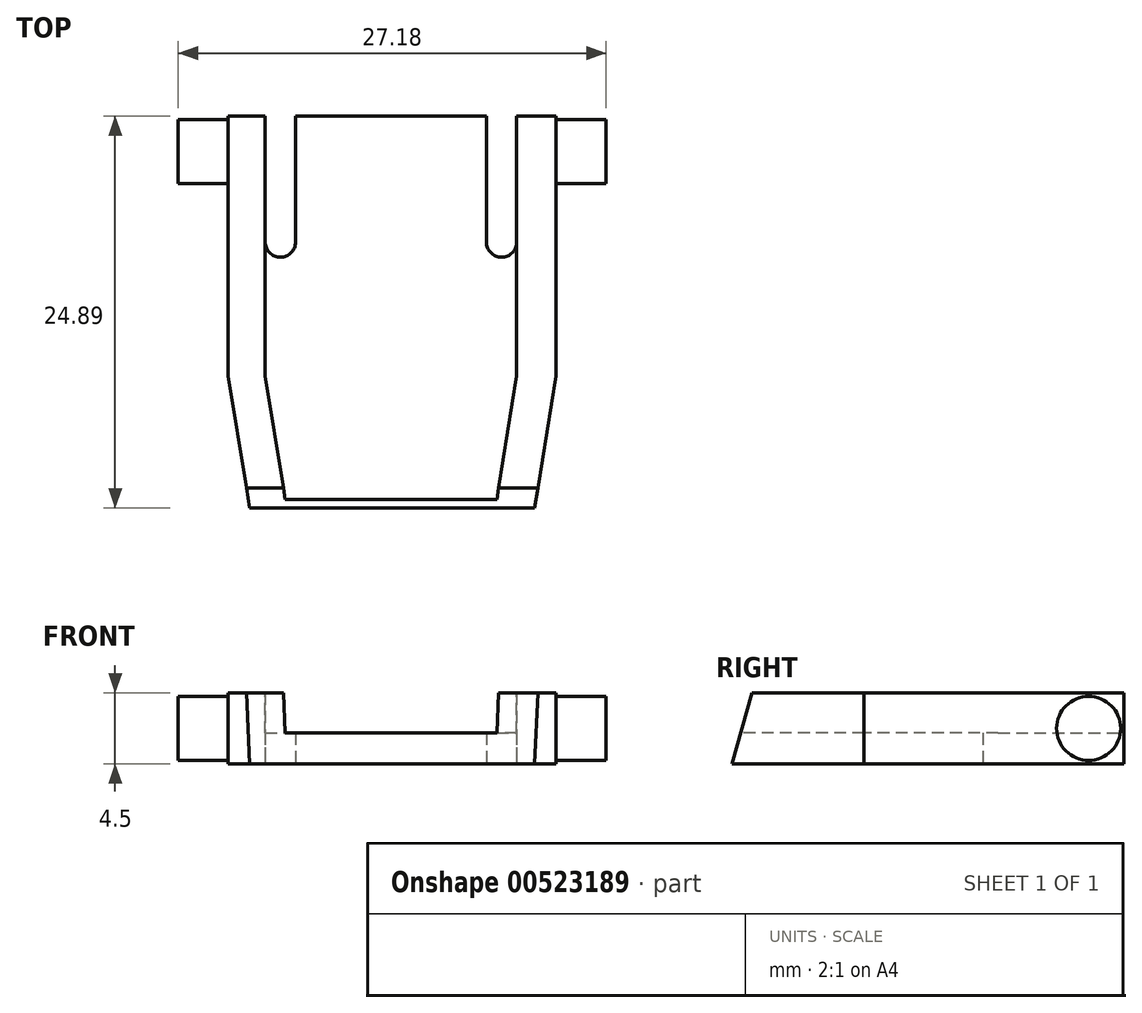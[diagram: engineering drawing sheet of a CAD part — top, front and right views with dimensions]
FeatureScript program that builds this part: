
annotation { "Feature Type Name" : "Feature", "Feature Type Description" : "" }
export const myFeature = defineFeature(function(context is Context, id is Id, definition is map)
    precondition{}
    {
        {
            var Q0;
            Q0=qCreatedBy(makeId("Top.planeOp"),FACE);
            var sketch = newSketch(context, id + "F0", { "sketchPlane" : qUnion([Q0])});
            skLineSegment(sketch, "E0.bottom", {"start": v(-13.75, -0.3) * mm, "end": v(-10.25, -0.3) * mm});
            skLineSegment(sketch, "E0.right", {"start": v(-10.25, -0.3) * mm, "end": v(-10.25, -18.09) * mm});
            skLineSegment(sketch, "E1.bottom", {"start": v(14.07, -0.3) * mm, "end": v(10.57, -0.3) * mm});
            skLineSegment(sketch, "E1.right", {"start": v(10.57, -0.3) * mm, "end": v(10.57, -18.09) * mm});
            skLineSegment(sketch, "E2.top", {"start": v(-6.94, -2.16) * mm, "end": v(-6.94, -2.16) * mm});
            skLineSegment(sketch, "E2.left", {"start": v(-7.9, 6.8) * mm, "end": v(-7.9, -1.2) * mm});
            skLineSegment(sketch, "E2.right", {"start": v(-5.97, 6.8) * mm, "end": v(-5.97, -1.2) * mm});
            skLineSegment(sketch, "E3.bottom", {"start": v(7.1, -2.16) * mm, "end": v(7.1, -2.16) * mm});
            skLineSegment(sketch, "E3.left", {"start": v(6.14, -1.2) * mm, "end": v(6.14, 6.8) * mm});
            skLineSegment(sketch, "E3.right", {"start": v(8.07, -1.2) * mm, "end": v(8.07, 6.8) * mm});
            skLineSegment(sketch, "E4", {"start": v(-13.75, 6.8) * mm, "end": v(-7.9, 6.8) * mm});
            skLineSegment(sketch, "E5", {"start": v(8.07, 6.8) * mm, "end": v(14.07, 6.8) * mm});
            skLineSegment(sketch, "E6", {"start": v(-5.97, 6.8) * mm, "end": v(6.14, 6.8) * mm});
            skLineSegment(sketch, "E7", {"start": v(14.07, 6.8) * mm, "end": v(14.07, -0.3) * mm});
            skLineSegment(sketch, "E8", {"start": v(-13.75, -0.3) * mm, "end": v(-13.75, 6.8) * mm});
            skLineSegment(sketch, "E9", {"start": v(-10.25, -9.7) * mm, "end": v(-8.9, -18.09) * mm});
            skLineSegment(sketch, "E10", {"start": v(-8.9, -18.09) * mm, "end": v(9.21, -18.09) * mm});
            skLineSegment(sketch, "E11", {"start": v(9.21, -18.09) * mm, "end": v(10.57, -9.7) * mm});
            skLineSegment(sketch, "E12", {"start": v(9.21, -18.09) * mm, "end": v(10.57, -18.09) * mm});
            skLineSegment(sketch, "E13", {"start": v(-8.9, -18.09) * mm, "end": v(-10.25, -18.09) * mm});
            skLineSegment(sketch, "E14.bottom", {"start": v(10.57, 6.8) * mm, "end": v(14.07, 6.8) * mm});
            skLineSegment(sketch, "E14.top", {"start": v(10.57, 5.97) * mm, "end": v(14.07, 5.97) * mm});
            skLineSegment(sketch, "E14.left", {"start": v(10.57, 6.8) * mm, "end": v(10.57, 5.97) * mm});
            skLineSegment(sketch, "E14.right", {"start": v(14.07, 6.8) * mm, "end": v(14.07, 5.97) * mm});
            skLineSegment(sketch, "E15.bottom", {"start": v(-13.75, 5.97) * mm, "end": v(-10.25, 5.97) * mm});
            skLineSegment(sketch, "E15.top", {"start": v(-13.75, 6.8) * mm, "end": v(-10.25, 6.8) * mm});
            skLineSegment(sketch, "E15.left", {"start": v(-13.75, 5.97) * mm, "end": v(-13.75, 6.8) * mm});
            skLineSegment(sketch, "E15.right", {"start": v(-10.25, 5.97) * mm, "end": v(-10.25, 6.8) * mm});
            skPoint(sketch, "E16.visualSharp", {"position": v(-7.9, -2.16) * mm});
            skArc(sketch, "E16.filletArc", {"start": v(-7.9, -1.2) * mm, "mid": v(-7.62, -1.88) * mm, "end": v(-6.94, -2.16) * mm});
            skPoint(sketch, "E17.visualSharp", {"position": v(-5.97, -2.16) * mm});
            skArc(sketch, "E17.filletArc", {"start": v(-6.94, -2.16) * mm, "mid": v(-6.26, -1.88) * mm, "end": v(-5.97, -1.2) * mm});
            skPoint(sketch, "E18.visualSharp", {"position": v(6.14, -2.16) * mm});
            skArc(sketch, "E18.filletArc", {"start": v(6.14, -1.2) * mm, "mid": v(6.42, -1.88) * mm, "end": v(7.1, -2.16) * mm});
            skPoint(sketch, "E19.visualSharp", {"position": v(8.07, -2.16) * mm});
            skArc(sketch, "E19.filletArc", {"start": v(7.1, -2.16) * mm, "mid": v(7.79, -1.88) * mm, "end": v(8.07, -1.2) * mm});
            skLineSegment(sketch, "E20", {"start": v(-10.25, 5.97) * mm, "end": v(-10.25, -0.3) * mm});
            skLineSegment(sketch, "E21", {"start": v(10.57, 5.97) * mm, "end": v(10.57, -0.3) * mm});
            skSolve(sketch);
        }
        {
            var Q0;
            Q0=makeQuery(id+"F0.imprint","IMPRINT",FACE,{"disambiguationData":[TD([[makeQuery(id+"F0.imprint","IMPRINT",EDGE,{"derivedFrom":sQuery(id+"F0.wireOp",EDGE,"E2.left")}),-1.0]])]});
            extrude(context, id + "F1", {"entities" : qUnion([Q0]), "depth" : 4.5 * mm, "offsetDistance" : 25.4 * mm});
        }
        {
            var Q0;
            Q0=makeQuery(id+"F1.opExtrude","SWEPT_FACE",FACE,{"disambiguationData":[OSD([sQuery(id+"F0.wireOp",EDGE,"E1.right"),sQuery(id+"F0.wireOp",EDGE,"E14.left"),sQuery(id+"F0.wireOp",EDGE,"E21")])]});
            var sketch = newSketch(context, id + "F2", { "sketchPlane" : qUnion([Q0])});
            skCircle(sketch, "E22", {"center": v(4.56, 2.25) * mm, "radius": 2.03 * mm});
            skLineSegment(sketch, "E23", {"start": v(4.56, 2.25) * mm, "end": v(4.56, 4.5) * mm});
            skLineSegment(sketch, "E24", {"start": v(4.56, 2.25) * mm, "end": v(4.56, 0) * mm});
            skLineSegment(sketch, "E25", {"start": v(4.56, 4.5) * mm, "end": v(4.56, 4.28) * mm});
            skLineSegment(sketch, "E26", {"start": v(6.8, 2.25) * mm, "end": v(6.59, 2.25) * mm});
            skSolve(sketch);
        }
        {
            var Q0;
            {var subQ0=sQuery(id+"F2.wireOp",EDGE,"E23");Q0=makeQuery(id+"F2.imprint","IMPRINT",FACE,{"disambiguationData":[TD([[makeQuery(id+"F2.imprint","IMPRINT",EDGE,{"derivedFrom":subQ0}),1.0]])]});}
            var Q1;
            {var subQ0=sQuery(id+"F2.wireOp",EDGE,"E23");Q1=makeQuery(id+"F2.imprint","IMPRINT",FACE,{"disambiguationData":[TD([[makeQuery(id+"F2.imprint","IMPRINT",EDGE,{"derivedFrom":subQ0}),-1.0]])]});}
            extrude(context, id + "F3", {"entities" : qUnion([Q0, Q1]), "operationType" : NewBodyOperationType.ADD, "depth" : 3.17 * mm, "offsetDistance" : 25.4 * mm});
        }
        {
            var Q0;
            Q0=makeQuery(id+"F1.opExtrude","SWEPT_FACE",FACE,{"disambiguationData":[OSD([sQuery(id+"F0.wireOp",EDGE,"E0.right"),sQuery(id+"F0.wireOp",EDGE,"E15.right"),sQuery(id+"F0.wireOp",EDGE,"E20")])]});
            var sketch = newSketch(context, id + "F4", { "sketchPlane" : qUnion([Q0])});
            skCircle(sketch, "E27", {"center": v(-4.56, 2.25) * mm, "radius": 2.03 * mm});
            skLineSegment(sketch, "E28", {"start": v(-4.56, 2.25) * mm, "end": v(-4.56, 4.5) * mm});
            skLineSegment(sketch, "E29", {"start": v(-4.56, 2.25) * mm, "end": v(-4.56, 0) * mm});
            skLineSegment(sketch, "E30", {"start": v(-6.8, 2.25) * mm, "end": v(-6.59, 2.25) * mm});
            skLineSegment(sketch, "E31", {"start": v(-4.56, 4.5) * mm, "end": v(-4.56, 4.28) * mm});
            skSolve(sketch);
        }
        {
            var Q0;
            {var subQ0=sQuery(id+"F4.wireOp",EDGE,"E28");Q0=makeQuery(id+"F4.imprint","IMPRINT",FACE,{"disambiguationData":[TD([[makeQuery(id+"F4.imprint","IMPRINT",EDGE,{"derivedFrom":subQ0}),1.0]])]});}
            var Q1;
            {var subQ0=sQuery(id+"F4.wireOp",EDGE,"E28");Q1=makeQuery(id+"F4.imprint","IMPRINT",FACE,{"disambiguationData":[TD([[makeQuery(id+"F4.imprint","IMPRINT",EDGE,{"derivedFrom":subQ0}),-1.0]])]});}
            extrude(context, id + "F5", {"entities" : qUnion([Q0, Q1]), "operationType" : NewBodyOperationType.ADD, "depth" : 3.17 * mm, "offsetDistance" : 25.4 * mm});
        }
        {
            var Q0;
            Q0=makeQuery(id+"F1.opExtrude","CAP_FACE",FACE,{"disambiguationData":[OSD([sQuery(id+"F0.wireOp",EDGE,"E0.right"),sQuery(id+"F0.wireOp",EDGE,"E1.right"),sQuery(id+"F0.wireOp",EDGE,"E2.left"),sQuery(id+"F0.wireOp",EDGE,"E2.right"),sQuery(id+"F0.wireOp",EDGE,"E3.left"),sQuery(id+"F0.wireOp",EDGE,"E3.right"),sQuery(id+"F0.wireOp",EDGE,"E4"),sQuery(id+"F0.wireOp",EDGE,"E5"),sQuery(id+"F0.wireOp",EDGE,"E6"),sQuery(id+"F0.wireOp",EDGE,"E9"),sQuery(id+"F0.wireOp",EDGE,"E10"),sQuery(id+"F0.wireOp",EDGE,"E11"),sQuery(id+"F0.wireOp",EDGE,"E14.left"),sQuery(id+"F0.wireOp",EDGE,"E15.right"),sQuery(id+"F0.wireOp",EDGE,"E16.filletArc"),sQuery(id+"F0.wireOp",EDGE,"E17.filletArc"),sQuery(id+"F0.wireOp",EDGE,"E18.filletArc"),sQuery(id+"F0.wireOp",EDGE,"E19.filletArc"),sQuery(id+"F0.wireOp",EDGE,"E20"),sQuery(id+"F0.wireOp",EDGE,"E21")])],"isStart":false});
            var sketch = newSketch(context, id + "F6", { "sketchPlane" : qUnion([Q0])});
            skLineSegment(sketch, "E32", {"start": v(-7.9, -1.2) * mm, "end": v(-7.9, -9.7) * mm});
            skLineSegment(sketch, "E33", {"start": v(-7.9, -9.7) * mm, "end": v(-6.55, -18.09) * mm});
            skLineSegment(sketch, "E34", {"start": v(8.07, -1.2) * mm, "end": v(8.07, -9.7) * mm});
            skLineSegment(sketch, "E35", {"start": v(8.07, -9.7) * mm, "end": v(6.71, -18.09) * mm});
            skSolve(sketch);
        }
        {
            var Q0;
            Q0=makeQuery(id+"F6.imprint","IMPRINT",FACE,{"disambiguationData":[TD([[makeQuery(id+"F6.imprint","IMPRINT",EDGE,{"derivedFrom":sQuery(id+"F6.wireOp",EDGE,"E32")}),1.0]])]});
            extrude(context, id + "F7", {"entities" : qUnion([Q0]), "operationType" : NewBodyOperationType.REMOVE, "oppositeDirection" : true, "depth" : 2.54 * mm, "offsetDistance" : 25.4 * mm});
        }
        {
            var Q0;
            Q0=makeQuery(id+"F1.opExtrude","SWEPT_FACE",FACE,{"disambiguationData":[OSD([sQuery(id+"F0.wireOp",EDGE,"E1.right"),sQuery(id+"F0.wireOp",EDGE,"E14.left"),sQuery(id+"F0.wireOp",EDGE,"E21")])]});
            var sketch = newSketch(context, id + "F8", { "sketchPlane" : qUnion([Q0])});
            skLineSegment(sketch, "E36.0.0", {"start": v(-18.09, 0) * mm, "end": v(-9.7, 0) * mm});
            skLineSegment(sketch, "E36.0.1", {"start": v(-9.7, 0) * mm, "end": v(-9.7, 4.5) * mm});
            skLineSegment(sketch, "E36.0.2", {"start": v(-9.7, 4.5) * mm, "end": v(-18.09, 4.5) * mm});
            skLineSegment(sketch, "E36.0.3", {"start": v(-18.09, 4.5) * mm, "end": v(-18.09, 0) * mm});
            skLineSegment(sketch, "E37", {"start": v(-18.09, 0) * mm, "end": v(-16.82, 4.5) * mm});
            skSolve(sketch);
        }
        {
            var Q0;
            {var subQ0=sQuery(id+"F8.wireOp",EDGE,"E36.0.3");Q0=makeQuery(id+"F8.imprint","IMPRINT",FACE,{"disambiguationData":[TD([[makeQuery(id+"F8.imprint","IMPRINT",EDGE,{"derivedFrom":subQ0}),1.0]])]});}
            extrude(context, id + "F9", {"entities" : qUnion([Q0]), "operationType" : NewBodyOperationType.REMOVE, "endBound" : BoundingType.THROUGH_ALL, "oppositeDirection" : true, "depth" : 25.4 * mm, "offsetDistance" : 25.4 * mm});
        }
    });
